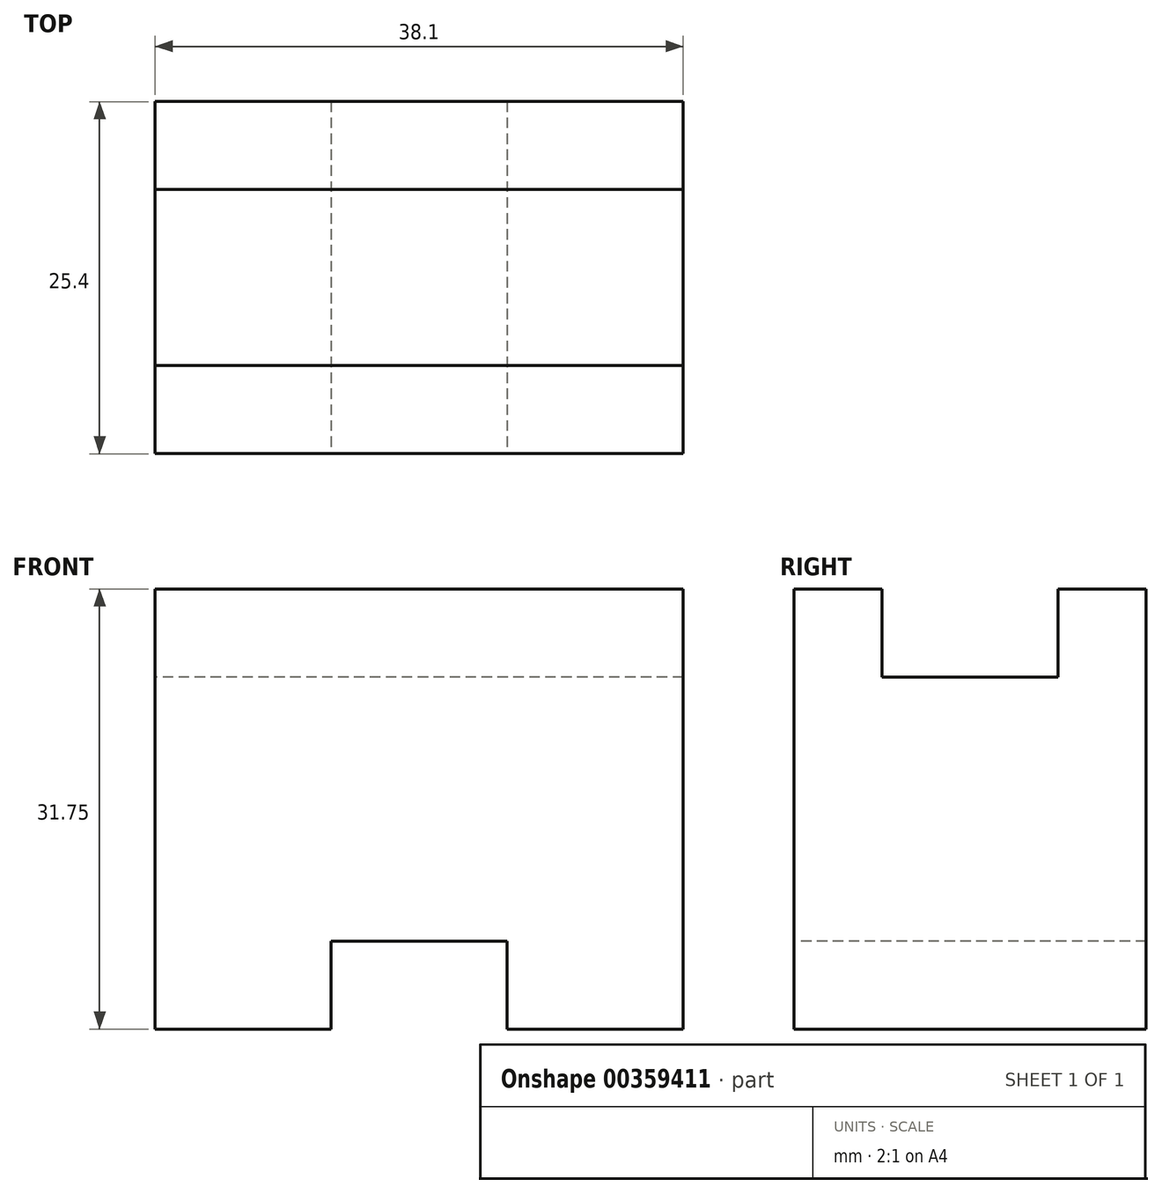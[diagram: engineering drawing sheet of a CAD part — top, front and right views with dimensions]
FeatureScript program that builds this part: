
annotation { "Feature Type Name" : "Feature", "Feature Type Description" : "" }
export const myFeature = defineFeature(function(context is Context, id is Id, definition is map)
    precondition{}
    {
        {
            var Q0;
            Q0=qCreatedBy(makeId("Right.planeOp"),FACE);
            var sketch = newSketch(context, id + "F0", { "sketchPlane" : qUnion([Q0])});
            skLineSegment(sketch, "E0", {"start": v(9.03, 0) * mm, "end": v(34.43, 0) * mm});
            skLineSegment(sketch, "E1", {"start": v(34.43, 0) * mm, "end": v(34.43, 31.75) * mm});
            skLineSegment(sketch, "E2", {"start": v(34.43, 31.75) * mm, "end": v(28.08, 31.75) * mm});
            skLineSegment(sketch, "E3", {"start": v(28.08, 31.75) * mm, "end": v(28.08, 25.4) * mm});
            skLineSegment(sketch, "E4", {"start": v(28.08, 25.4) * mm, "end": v(15.38, 25.4) * mm});
            skLineSegment(sketch, "E5", {"start": v(15.38, 25.4) * mm, "end": v(15.38, 31.75) * mm});
            skLineSegment(sketch, "E6", {"start": v(15.38, 31.75) * mm, "end": v(9.03, 31.75) * mm});
            skLineSegment(sketch, "E7", {"start": v(9.03, 31.75) * mm, "end": v(9.03, 0) * mm});
            skSolve(sketch);
        }
        {
            var Q0;
            Q0=makeQuery(id+"F0.imprint","IMPRINT",FACE,{"disambiguationData":[TD([[makeQuery(id+"F0.imprint","IMPRINT",EDGE,{"derivedFrom":sQuery(id+"F0.wireOp",EDGE,"E0")}),1.0]])]});
            extrude(context, id + "F1", {"entities" : qUnion([Q0]), "depth" : 38.1 * mm});
        }
        {
            var Q0;
            Q0=makeQuery(id+"F1.opExtrude","SWEPT_FACE",FACE,{"disambiguationData":[OSD([sQuery(id+"F0.wireOp",EDGE,"E7")])]});
            var sketch = newSketch(context, id + "F2", { "sketchPlane" : qUnion([Q0])});
            skLineSegment(sketch, "E8", {"start": v(12.7, 0) * mm, "end": v(12.7, 6.35) * mm});
            skLineSegment(sketch, "E9", {"start": v(12.7, 6.35) * mm, "end": v(25.4, 6.35) * mm});
            skLineSegment(sketch, "E10", {"start": v(25.4, 6.35) * mm, "end": v(25.4, 0) * mm});
            skLineSegment(sketch, "E11", {"start": v(0, 0) * mm, "end": v(12.7, 0) * mm});
            skLineSegment(sketch, "E12", {"start": v(25.4, 0) * mm, "end": v(38.1, 0) * mm});
            skSolve(sketch);
        }
        {
            var Q0;
            Q0 = qSketchRegion(id + "F2", true);
            var Q1;
            {var subQ0=sQuery(id+"F2.wireOp",EDGE,"E8");Q1=makeQuery(id+"F2.imprint","IMPRINT",FACE,{"disambiguationData":[TD([[makeQuery(id+"F2.imprint","IMPRINT",EDGE,{"derivedFrom":subQ0}),-1.0]])]});}
            extrude(context, id + "F3", {"entities" : qUnion([Q0, Q1]), "operationType" : NewBodyOperationType.REMOVE, "oppositeDirection" : true, "depth" : 25.4 * mm});
        }
    });
